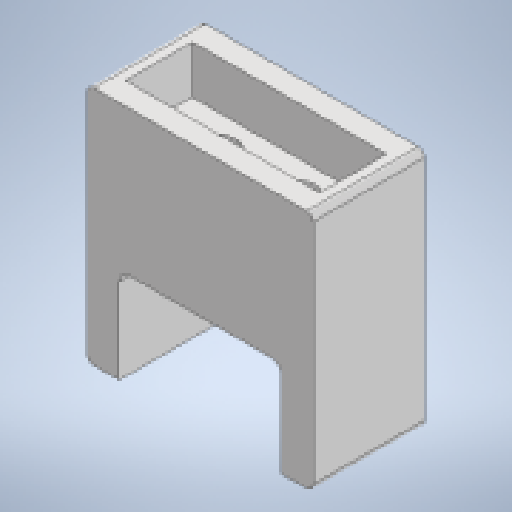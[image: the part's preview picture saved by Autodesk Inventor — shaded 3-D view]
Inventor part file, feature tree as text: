
AUTODESK INVENTOR PART (.ipt)
format: ipt  version: 2023 (Build 270158000, 158)  size: 197,120 bytes
history: native  units: in
note: dims shown in document units (in); Inventor stores cm internally (conversion verified against a paired STEP export)
features: extrude x6, sketch x5, fillet x2
ambient origin geometry x8: Origin, YZ Plane, XZ Plane, XY Plane, X Axis, Y Axis, Z Axis, Center Point
bodies: Solid1 (feature_tree)
feature tree (13):
  sketch  "Sketch1"  dims[d0=0.7874in d1=2.3622in]
  extrude  "Extrusion1"  Depth=2.3622in
  extrude  "Extrusion2"  Depth=0.0197in
  extrude  "Extrusion3"  Depth=0.0197in
  extrude  "Extrusion4"  Depth=1.811in
  extrude  "Extrusion5"  Depth=1.378in
  extrude  "Extrusion6"  Depth=0.3937in TaperAngle=0.0deg
  fillet  "Fillet1"  Radius=1.3937in
  fillet  "Fillet2"  Radius=0.3937in
  sketch  "Sketch2"  dims[d2=0.0197in d3=0.0197in]
  sketch  "Sketch3"  dims[d4=0.0197in d5=0.0197in]
  sketch  "Sketch4"  dims[d6=0.1417in d7=1.811in]
  sketch  "Sketch5"  dims[d9=2.7874in d10=1.378in d11=0.3937in d12=0.0in d13=1.3937in d14=0.0in d15=0.3937in d16=0.1969in d17=0.0in d18=0.0in d19=0.3937in d20=1.1969in d21=0.0in d22=0.0in d23=2.0in d24=0.125in d25=0.3937in d26=1.1811in d27=0.3937in d28=0.0in d29=0.2362in d30=0.9843in d31=0.3937in d32=0.0in d34=0.4724in d35=0.3937in d36=0.0in d37=0.0787in d38=0.0787in]
